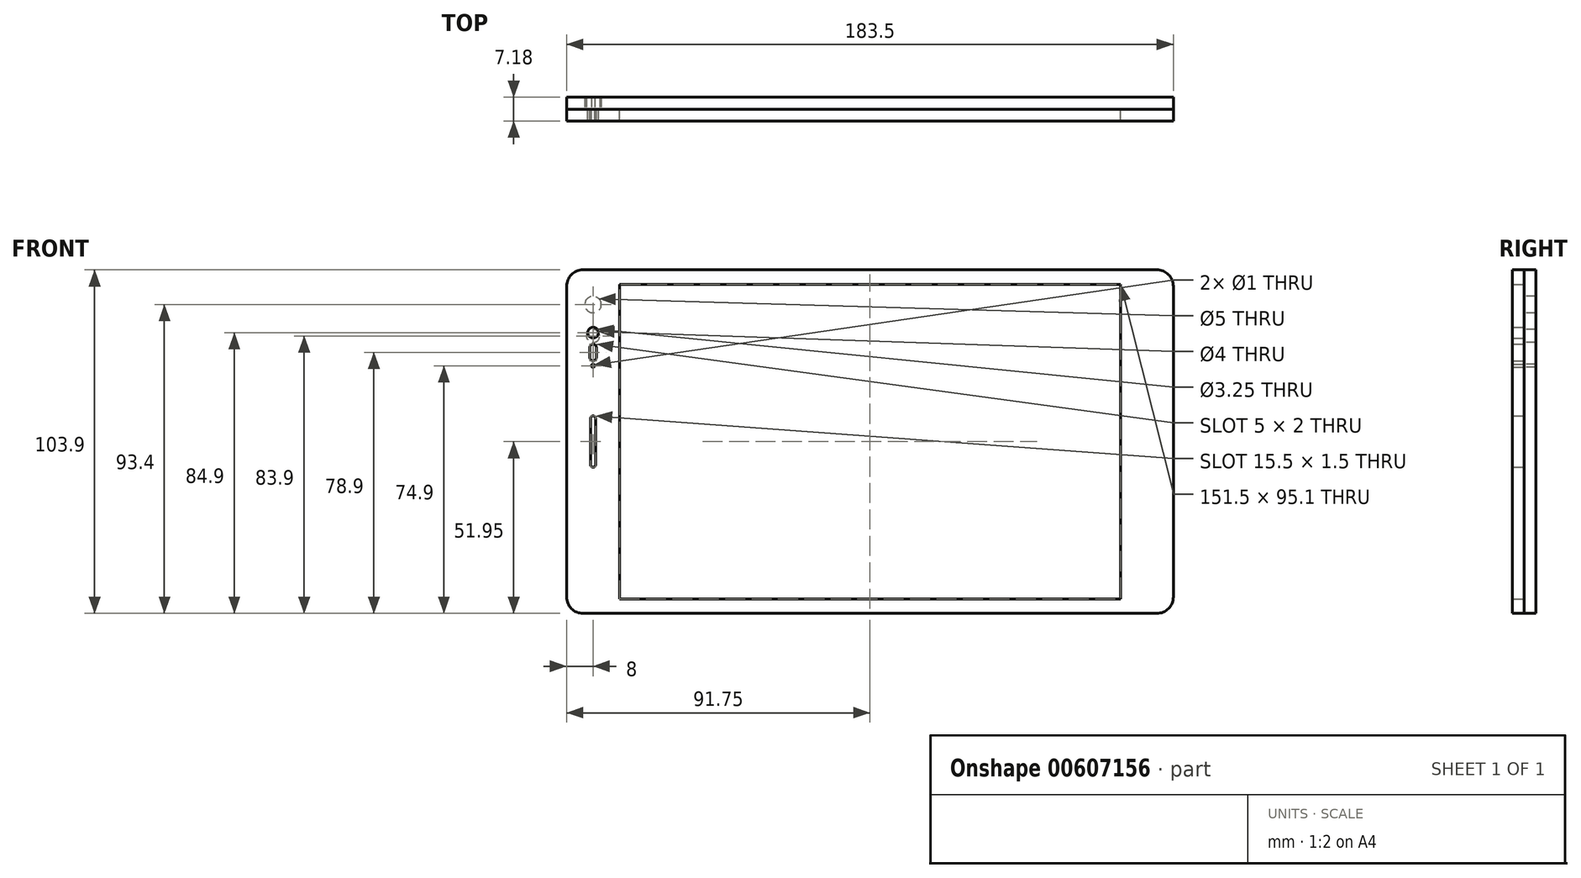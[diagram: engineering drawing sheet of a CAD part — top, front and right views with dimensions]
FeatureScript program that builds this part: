
annotation { "Feature Type Name" : "Feature", "Feature Type Description" : "" }
export const myFeature = defineFeature(function(context is Context, id is Id, definition is map)
    precondition{}
    {
        {
            var Q0;
            Q0=qCreatedBy(makeId("Front.planeOp"),FACE);
            var sketch = newSketch(context, id + "F0", { "sketchPlane" : qUnion([Q0])});
            skLineSegment(sketch, "E0.bottom", {"start": v(-130.5, 51.95) * mm, "end": v(43, 51.95) * mm});
            skLineSegment(sketch, "E0.top", {"start": v(-130.5, -51.95) * mm, "end": v(43, -51.95) * mm});
            skLineSegment(sketch, "E0.left", {"start": v(-135.5, 46.95) * mm, "end": v(-135.5, -46.95) * mm});
            skLineSegment(sketch, "E0.right", {"start": v(48, 46.95) * mm, "end": v(48, -46.95) * mm});
            skPoint(sketch, "E1.visualSharp", {"position": v(-135.5, 51.95) * mm});
            skArc(sketch, "E1.filletArc", {"start": v(-130.5, 51.95) * mm, "mid": v(-134.04, 50.49) * mm, "end": v(-135.5, 46.95) * mm});
            skPoint(sketch, "E2.visualSharp", {"position": v(48, 51.95) * mm});
            skArc(sketch, "E2.filletArc", {"start": v(48, 46.95) * mm, "mid": v(46.54, 50.49) * mm, "end": v(43, 51.95) * mm});
            skPoint(sketch, "E3.visualSharp", {"position": v(48, -51.95) * mm});
            skArc(sketch, "E3.filletArc", {"start": v(43, -51.95) * mm, "mid": v(46.54, -50.49) * mm, "end": v(48, -46.95) * mm});
            skPoint(sketch, "E4.visualSharp", {"position": v(-135.5, -51.95) * mm});
            skArc(sketch, "E4.filletArc", {"start": v(-135.5, -46.95) * mm, "mid": v(-134.04, -50.49) * mm, "end": v(-130.5, -51.95) * mm});
            skLineSegment(sketch, "E5.bottom", {"start": v(-119.5, 47.55) * mm, "end": v(32, 47.55) * mm});
            skLineSegment(sketch, "E5.top", {"start": v(-119.5, -47.55) * mm, "end": v(32, -47.55) * mm});
            skLineSegment(sketch, "E5.left", {"start": v(-119.5, 47.55) * mm, "end": v(-119.5, -47.55) * mm});
            skLineSegment(sketch, "E5.right", {"start": v(32, 47.55) * mm, "end": v(32, -47.55) * mm});
            skCircle(sketch, "E6", {"center": v(-127.5, 32.95) * mm, "radius": 1.63 * mm});
            skLineSegment(sketch, "E7", {"start": v(-127.5, 51.95) * mm, "end": v(-127.5, -51.95) * mm, "construction": true});
            skLineSegment(sketch, "E8.bottom", {"start": v(-127.5, -7.75) * mm, "end": v(-127.5, -7.75) * mm});
            skLineSegment(sketch, "E8.top", {"start": v(-127.5, 7.75) * mm, "end": v(-127.5, 7.75) * mm});
            skLineSegment(sketch, "E8.left", {"start": v(-126.75, -7) * mm, "end": v(-126.75, 7) * mm});
            skLineSegment(sketch, "E8.right", {"start": v(-128.25, -7) * mm, "end": v(-128.25, 7) * mm});
            skPoint(sketch, "E8.middle", {"position": v(-127.5, 0) * mm});
            skLineSegment(sketch, "E9.bottom", {"start": v(-127.5, 24.45) * mm, "end": v(-127.5, 24.45) * mm});
            skLineSegment(sketch, "E9.top", {"start": v(-127.5, 29.45) * mm, "end": v(-127.5, 29.45) * mm});
            skLineSegment(sketch, "E9.left", {"start": v(-126.5, 25.45) * mm, "end": v(-126.5, 28.45) * mm});
            skLineSegment(sketch, "E9.right", {"start": v(-128.5, 25.45) * mm, "end": v(-128.5, 28.45) * mm});
            skPoint(sketch, "E9.middle", {"position": v(-127.5, 26.95) * mm});
            skPoint(sketch, "E10.visualSharp", {"position": v(-128.25, 7.75) * mm});
            skArc(sketch, "E10.filletArc", {"start": v(-127.5, 7.75) * mm, "mid": v(-128.03, 7.53) * mm, "end": v(-128.25, 7) * mm});
            skPoint(sketch, "E11.visualSharp", {"position": v(-126.75, 7.75) * mm});
            skArc(sketch, "E11.filletArc", {"start": v(-126.75, 7) * mm, "mid": v(-126.97, 7.53) * mm, "end": v(-127.5, 7.75) * mm});
            skPoint(sketch, "E12.visualSharp", {"position": v(-128.25, -7.75) * mm});
            skArc(sketch, "E12.filletArc", {"start": v(-128.25, -7) * mm, "mid": v(-128.03, -7.53) * mm, "end": v(-127.5, -7.75) * mm});
            skPoint(sketch, "E13.visualSharp", {"position": v(-126.75, -7.75) * mm});
            skArc(sketch, "E13.filletArc", {"start": v(-127.5, -7.75) * mm, "mid": v(-126.97, -7.53) * mm, "end": v(-126.75, -7) * mm});
            skPoint(sketch, "E14.visualSharp", {"position": v(-128.5, 29.45) * mm});
            skArc(sketch, "E14.filletArc", {"start": v(-127.5, 29.45) * mm, "mid": v(-128.2, 29.16) * mm, "end": v(-128.5, 28.45) * mm});
            skPoint(sketch, "E15.visualSharp", {"position": v(-126.5, 29.45) * mm});
            skArc(sketch, "E15.filletArc", {"start": v(-126.5, 28.45) * mm, "mid": v(-126.8, 29.16) * mm, "end": v(-127.5, 29.45) * mm});
            skPoint(sketch, "E16.visualSharp", {"position": v(-126.5, 24.45) * mm});
            skArc(sketch, "E16.filletArc", {"start": v(-127.5, 24.45) * mm, "mid": v(-126.8, 24.74) * mm, "end": v(-126.5, 25.45) * mm});
            skPoint(sketch, "E17.visualSharp", {"position": v(-128.5, 24.45) * mm});
            skArc(sketch, "E17.filletArc", {"start": v(-128.5, 25.45) * mm, "mid": v(-128.2, 24.74) * mm, "end": v(-127.5, 24.45) * mm});
            skCircle(sketch, "E18", {"center": v(-127.5, 41.45) * mm, "radius": 2.5 * mm});
            skCircle(sketch, "E19", {"center": v(-127.5, 31.95) * mm, "radius": 2 * mm});
            skCircle(sketch, "E20", {"center": v(-127.5, 22.95) * mm, "radius": 0.5 * mm});
            skSolve(sketch);
        }
        {
            var Q0;
            Q0=makeQuery(id+"F0.imprint","IMPRINT",FACE,{"disambiguationData":[TD([[makeQuery(id+"F0.imprint","IMPRINT",EDGE,{"derivedFrom":sQuery(id+"F0.wireOp",EDGE,"E0.bottom")}),-1.0]])]});
            var Q1;
            Q1=makeQuery(id+"F0.imprint","IMPRINT",FACE,{"disambiguationData":[TD([[makeQuery(id+"F0.imprint","IMPRINT",EDGE,{"derivedFrom":sQuery(id+"F0.wireOp",EDGE,"E18")}),1.0]])]});
            var Q2;
            {var subQ0=sQuery(id+"F0.wireOp",EDGE,"E19");var subQ1=sQuery(id+"F0.wireOp",EDGE,"E6");var subQ2=makeQuery(id+"F0.imprint","INTERSECT",VERTEX,{"disambiguationData":[OD(0.0)],"derivedFrom":[subQ1,subQ0]});Q2=makeQuery(id+"F0.imprint","IMPRINT",FACE,{"disambiguationData":[TD([[makeQuery(id+"F0.imprint","IMPRINT",EDGE,{"disambiguationData":[TD([[subQ2,-1.0]])],"derivedFrom":subQ1}),-1.0]])]});}
            extrude(context, id + "F1", {"entities" : qUnion([Q0, Q1, Q2]), "depth" : 3.59 * mm, "offsetDistance" : 25 * mm});
        }
        {
            var Q0;
            Q0=makeQuery(id+"F0.imprint","IMPRINT",FACE,{"disambiguationData":[TD([[makeQuery(id+"F0.imprint","IMPRINT",EDGE,{"derivedFrom":sQuery(id+"F0.wireOp",EDGE,"E6")}),1.0]])]});
            var Q1;
            Q1=makeQuery(id+"F0.imprint","IMPRINT",FACE,{"disambiguationData":[TD([[makeQuery(id+"F0.imprint","IMPRINT",EDGE,{"derivedFrom":sQuery(id+"F0.wireOp",EDGE,"E9.left")}),1.0]])]});
            var Q2;
            Q2=makeQuery(id+"F0.imprint","IMPRINT",FACE,{"disambiguationData":[TD([[makeQuery(id+"F0.imprint","IMPRINT",EDGE,{"derivedFrom":sQuery(id+"F0.wireOp",EDGE,"E5.bottom")}),-1.0]])]});
            var Q3;
            Q3=makeQuery(id+"F0.imprint","IMPRINT",FACE,{"disambiguationData":[TD([[makeQuery(id+"F0.imprint","IMPRINT",EDGE,{"derivedFrom":sQuery(id+"F0.wireOp",EDGE,"E8.left")}),1.0]])]});
            var Q4;
            Q4=makeQuery(id+"F0.imprint","IMPRINT",FACE,{"disambiguationData":[TD([[makeQuery(id+"F0.imprint","IMPRINT",EDGE,{"derivedFrom":sQuery(id+"F0.wireOp",EDGE,"E20")}),1.0]])]});
            var Q5;
            Q5=makeQuery(id+"F1.opExtrude","CAP_FACE",FACE,{"disambiguationData":[OSD([sQuery(id+"F0.wireOp",EDGE,"E0.bottom"),sQuery(id+"F0.wireOp",EDGE,"E0.top"),sQuery(id+"F0.wireOp",EDGE,"E0.left"),sQuery(id+"F0.wireOp",EDGE,"E0.right"),sQuery(id+"F0.wireOp",EDGE,"E1.filletArc"),sQuery(id+"F0.wireOp",EDGE,"E2.filletArc"),sQuery(id+"F0.wireOp",EDGE,"E3.filletArc"),sQuery(id+"F0.wireOp",EDGE,"E4.filletArc"),sQuery(id+"F0.wireOp",EDGE,"E5.bottom"),sQuery(id+"F0.wireOp",EDGE,"E5.top"),sQuery(id+"F0.wireOp",EDGE,"E5.left"),sQuery(id+"F0.wireOp",EDGE,"E5.right"),sQuery(id+"F0.wireOp",EDGE,"E6"),sQuery(id+"F0.wireOp",EDGE,"E8.left"),sQuery(id+"F0.wireOp",EDGE,"E8.right"),sQuery(id+"F0.wireOp",EDGE,"E9.left"),sQuery(id+"F0.wireOp",EDGE,"E9.right"),sQuery(id+"F0.wireOp",EDGE,"E10.filletArc"),sQuery(id+"F0.wireOp",EDGE,"E11.filletArc"),sQuery(id+"F0.wireOp",EDGE,"E12.filletArc"),sQuery(id+"F0.wireOp",EDGE,"E13.filletArc"),sQuery(id+"F0.wireOp",EDGE,"E14.filletArc"),sQuery(id+"F0.wireOp",EDGE,"E15.filletArc"),sQuery(id+"F0.wireOp",EDGE,"E16.filletArc"),sQuery(id+"F0.wireOp",EDGE,"E17.filletArc")])],"isStart":false});
            extrude(context, id + "F2", {"entities" : qUnion([Q0, Q1, Q2, Q3, Q4]), "endBound" : BoundingType.UP_TO_SURFACE, "depth" : 25 * mm, "endBoundEntityFace" : qUnion([Q5]), "offsetDistance" : 5 * mm});
        }
        {
            var Q0;
            {var subQ0=sQuery(id+"F0.wireOp",EDGE,"E19");var subQ1=sQuery(id+"F0.wireOp",EDGE,"E6");var subQ2=makeQuery(id+"F0.imprint","INTERSECT",VERTEX,{"disambiguationData":[OD(0.0)],"derivedFrom":[subQ1,subQ0]});Q0=makeQuery(id+"F0.imprint","IMPRINT",FACE,{"disambiguationData":[TD([[makeQuery(id+"F0.imprint","IMPRINT",EDGE,{"disambiguationData":[TD([[subQ2,1.0]])],"derivedFrom":subQ1}),1.0]])]});}
            var Q1;
            Q1=makeQuery(id+"F0.imprint","IMPRINT",FACE,{"disambiguationData":[TD([[makeQuery(id+"F0.imprint","IMPRINT",EDGE,{"derivedFrom":sQuery(id+"F0.wireOp",EDGE,"E5.bottom")}),-1.0]])]});
            var Q2;
            Q2=makeQuery(id+"F0.imprint","IMPRINT",FACE,{"disambiguationData":[TD([[makeQuery(id+"F0.imprint","IMPRINT",EDGE,{"derivedFrom":sQuery(id+"F0.wireOp",EDGE,"E9.left")}),1.0]])]});
            var Q3;
            Q3=makeQuery(id+"F0.imprint","IMPRINT",FACE,{"disambiguationData":[TD([[makeQuery(id+"F0.imprint","IMPRINT",EDGE,{"derivedFrom":sQuery(id+"F0.wireOp",EDGE,"E8.left")}),1.0]])]});
            var Q4;
            Q4=makeQuery(id+"F0.imprint","IMPRINT",FACE,{"disambiguationData":[TD([[makeQuery(id+"F0.imprint","IMPRINT",EDGE,{"derivedFrom":sQuery(id+"F0.wireOp",EDGE,"E0.bottom")}),-1.0]])]});
            extrude(context, id + "F3", {"entities" : qUnion([Q0, Q1, Q2, Q3, Q4]), "oppositeDirection" : true, "depth" : 3.59 * mm, "offsetDistance" : 25 * mm});
        }
        {
            var Q0;
            Q0=makeQuery(id+"F0.imprint","IMPRINT",FACE,{"disambiguationData":[TD([[makeQuery(id+"F0.imprint","IMPRINT",EDGE,{"derivedFrom":sQuery(id+"F0.wireOp",EDGE,"E18")}),1.0]])]});
            var Q1;
            {var subQ0=sQuery(id+"F0.wireOp",EDGE,"E19");var subQ1=sQuery(id+"F0.wireOp",EDGE,"E6");var subQ2=makeQuery(id+"F0.imprint","INTERSECT",VERTEX,{"disambiguationData":[OD(0.0)],"derivedFrom":[subQ1,subQ0]});Q1=makeQuery(id+"F0.imprint","IMPRINT",FACE,{"disambiguationData":[TD([[makeQuery(id+"F0.imprint","IMPRINT",EDGE,{"disambiguationData":[TD([[subQ2,-1.0]])],"derivedFrom":subQ1}),-1.0]])]});}
            var Q2;
            {var subQ0=sQuery(id+"F0.wireOp",EDGE,"E19");var subQ1=sQuery(id+"F0.wireOp",EDGE,"E6");var subQ2=makeQuery(id+"F0.imprint","INTERSECT",VERTEX,{"disambiguationData":[OD(0.0)],"derivedFrom":[subQ1,subQ0]});Q2=makeQuery(id+"F0.imprint","IMPRINT",FACE,{"disambiguationData":[TD([[makeQuery(id+"F0.imprint","IMPRINT",EDGE,{"disambiguationData":[TD([[subQ2,-1.0]])],"derivedFrom":subQ1}),1.0]])]});}
            var Q3;
            Q3=makeQuery(id+"F3.opExtrude","CAP_FACE",FACE,{"disambiguationData":[OSD([sQuery(id+"F0.wireOp",EDGE,"E0.bottom"),sQuery(id+"F0.wireOp",EDGE,"E0.top"),sQuery(id+"F0.wireOp",EDGE,"E0.left"),sQuery(id+"F0.wireOp",EDGE,"E0.right"),sQuery(id+"F0.wireOp",EDGE,"E1.filletArc"),sQuery(id+"F0.wireOp",EDGE,"E2.filletArc"),sQuery(id+"F0.wireOp",EDGE,"E3.filletArc"),sQuery(id+"F0.wireOp",EDGE,"E4.filletArc"),sQuery(id+"F0.wireOp",EDGE,"E18"),sQuery(id+"F0.wireOp",EDGE,"E19")])],"isStart":false});
            extrude(context, id + "F4", {"entities" : qUnion([Q0, Q1, Q2]), "endBound" : BoundingType.UP_TO_SURFACE, "oppositeDirection" : true, "depth" : 25 * mm, "endBoundEntityFace" : qUnion([Q3]), "offsetDistance" : 25 * mm});
        }
    });
